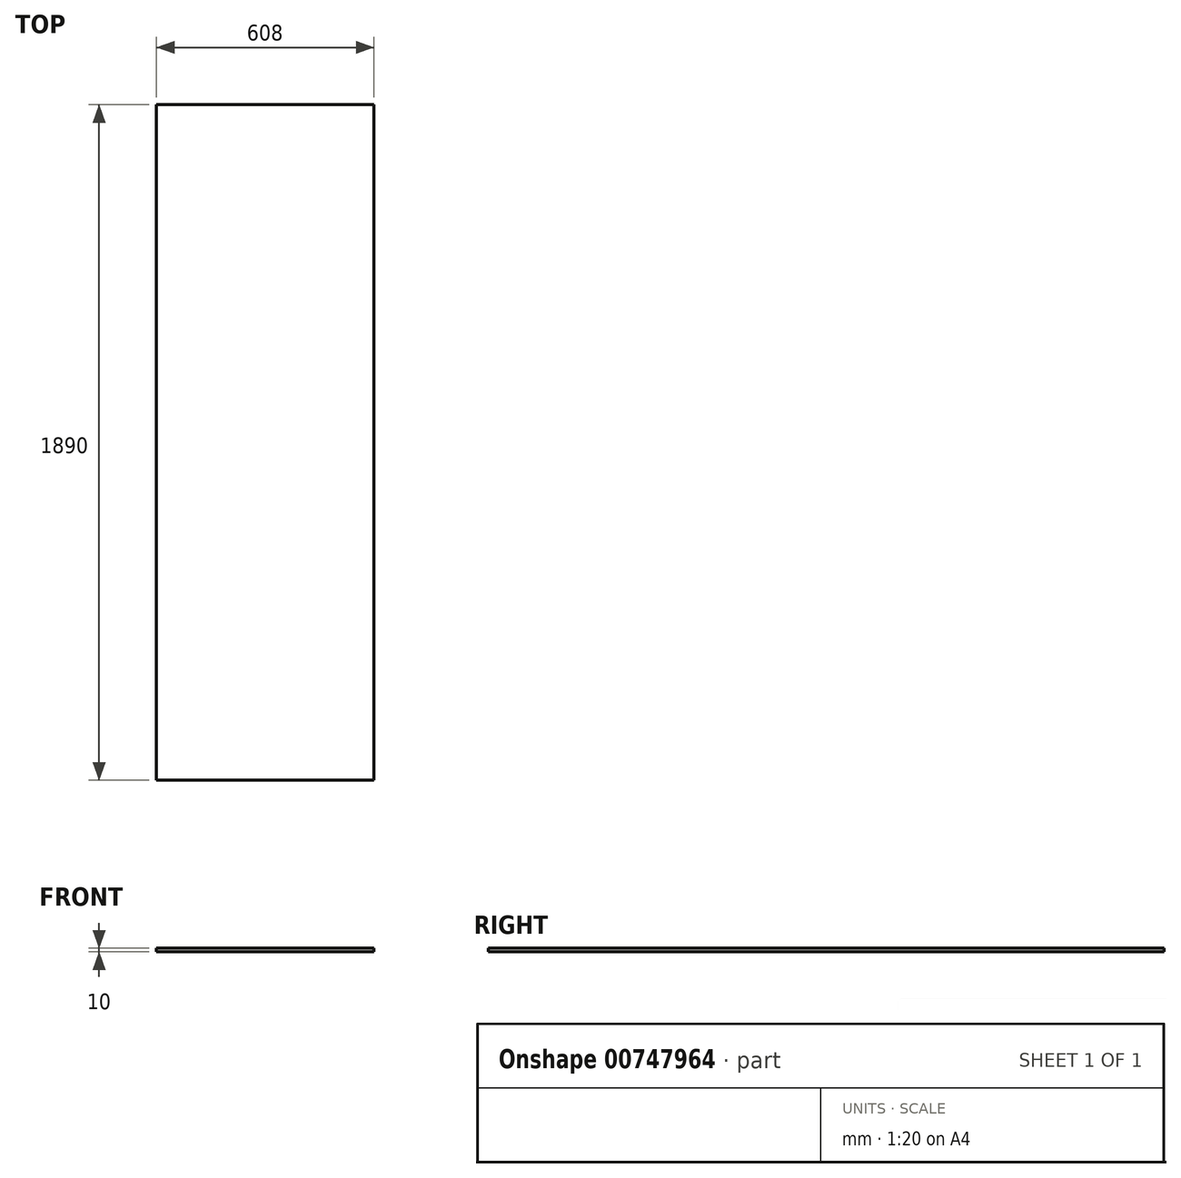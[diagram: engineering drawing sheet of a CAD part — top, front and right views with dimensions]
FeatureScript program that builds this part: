
annotation { "Feature Type Name" : "Feature", "Feature Type Description" : "" }
export const myFeature = defineFeature(function(context is Context, id is Id, definition is map)
    precondition{}
    {
        {
            var Q0;
            Q0=qCreatedBy(makeId("Front.planeOp"),FACE);
            var sketch = newSketch(context, id + "F0", { "sketchPlane" : qUnion([Q0])});
            skLineSegment(sketch, "E0.bottom", {"start": v(-508.43, -4.36) * mm, "end": v(99.57, -4.36) * mm});
            skLineSegment(sketch, "E0.top", {"start": v(-508.43, -14.36) * mm, "end": v(99.57, -14.36) * mm});
            skLineSegment(sketch, "E0.left", {"start": v(-508.43, -4.36) * mm, "end": v(-508.43, -14.36) * mm});
            skLineSegment(sketch, "E0.right", {"start": v(99.57, -4.36) * mm, "end": v(99.57, -14.36) * mm});
            skSolve(sketch);
        }
        {
            var Q0;
            Q0=makeQuery(id+"F0.imprint","IMPRINT",FACE,{"disambiguationData":[TD([[makeQuery(id+"F0.imprint","IMPRINT",EDGE,{"derivedFrom":sQuery(id+"F0.wireOp",EDGE,"E0.bottom")}),-1.0]])]});
            extrude(context, id + "F1", {"entities" : qUnion([Q0]), "depth" : 1890 * mm, "offsetDistance" : 25 * mm});
        }
    });
